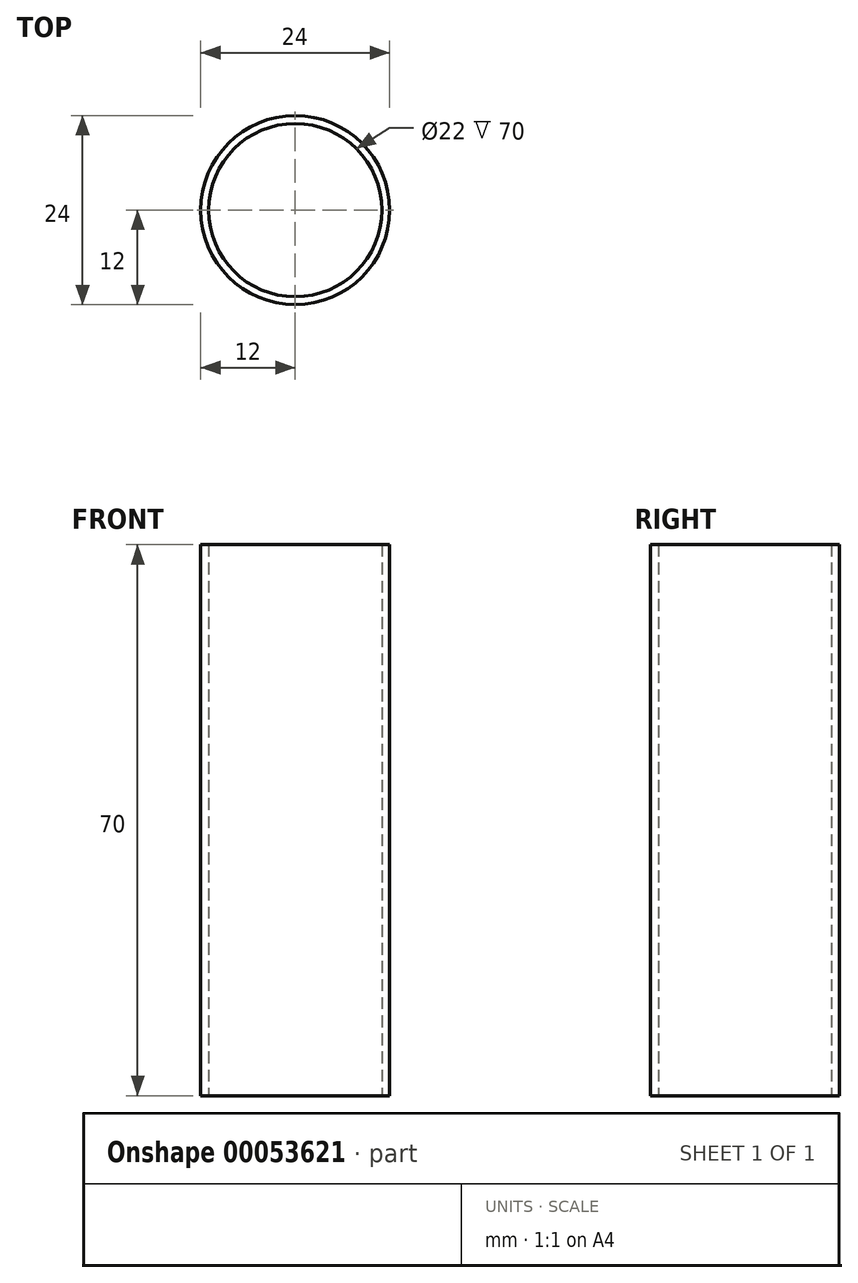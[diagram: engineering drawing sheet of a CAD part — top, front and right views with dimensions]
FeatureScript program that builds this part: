
annotation { "Feature Type Name" : "Feature", "Feature Type Description" : "" }
export const myFeature = defineFeature(function(context is Context, id is Id, definition is map)
    precondition{}
    {
        {
            var Q0;
            Q0=qCreatedBy(makeId("Top.planeOp"),FACE);
            var sketch = newSketch(context, id + "F0", { "sketchPlane" : qUnion([Q0])});
            skCircle(sketch, "E0", {"center": v(0, 0) * mm, "radius": 11 * mm});
            skCircle(sketch, "E1", {"center": v(0, 0) * mm, "radius": 12 * mm});
            skSolve(sketch);
        }
        {
            var Q0;
            Q0=makeQuery(id+"F0.imprint","IMPRINT",FACE,{"disambiguationData":[TD([[makeQuery(id+"F0.imprint","IMPRINT",EDGE,{"derivedFrom":sQuery(id+"F0.wireOp",EDGE,"E0")}),-1.0]])]});
            extrude(context, id + "F1", {"entities" : qUnion([Q0]), "depth" : 70 * mm});
        }
    });
